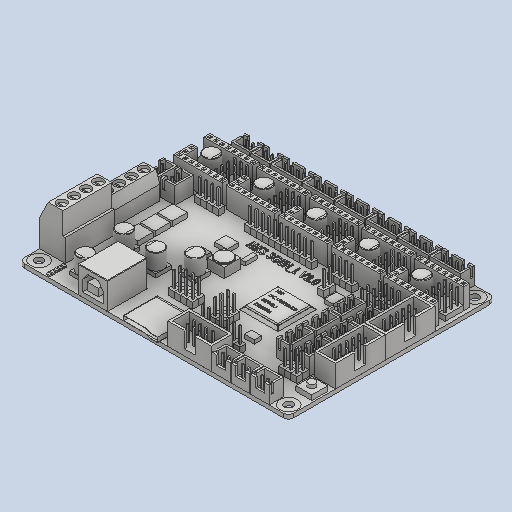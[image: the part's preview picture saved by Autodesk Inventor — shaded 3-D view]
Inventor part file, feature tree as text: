
AUTODESK INVENTOR PART (.ipt)
format: ipt  version: 2023 (Build 270158000, 158)  size: 2,914,816 bytes
history: native  units: mm
features: fillet x1
ambient origin geometry x8: Origin, YZ Plane, XZ Plane, XY Plane, X Axis, Y Axis, Z Axis, Center Point
bodies: Solid1 (feature_tree)
feature tree (1):
  fillet  "Fillet10"  [1 undecoded]
note: 1 required parameter value undecoded (feature->parameter linkage not recoverable at this tier; creation-order binding heuristic only, values carry confidence <= 0.55)
